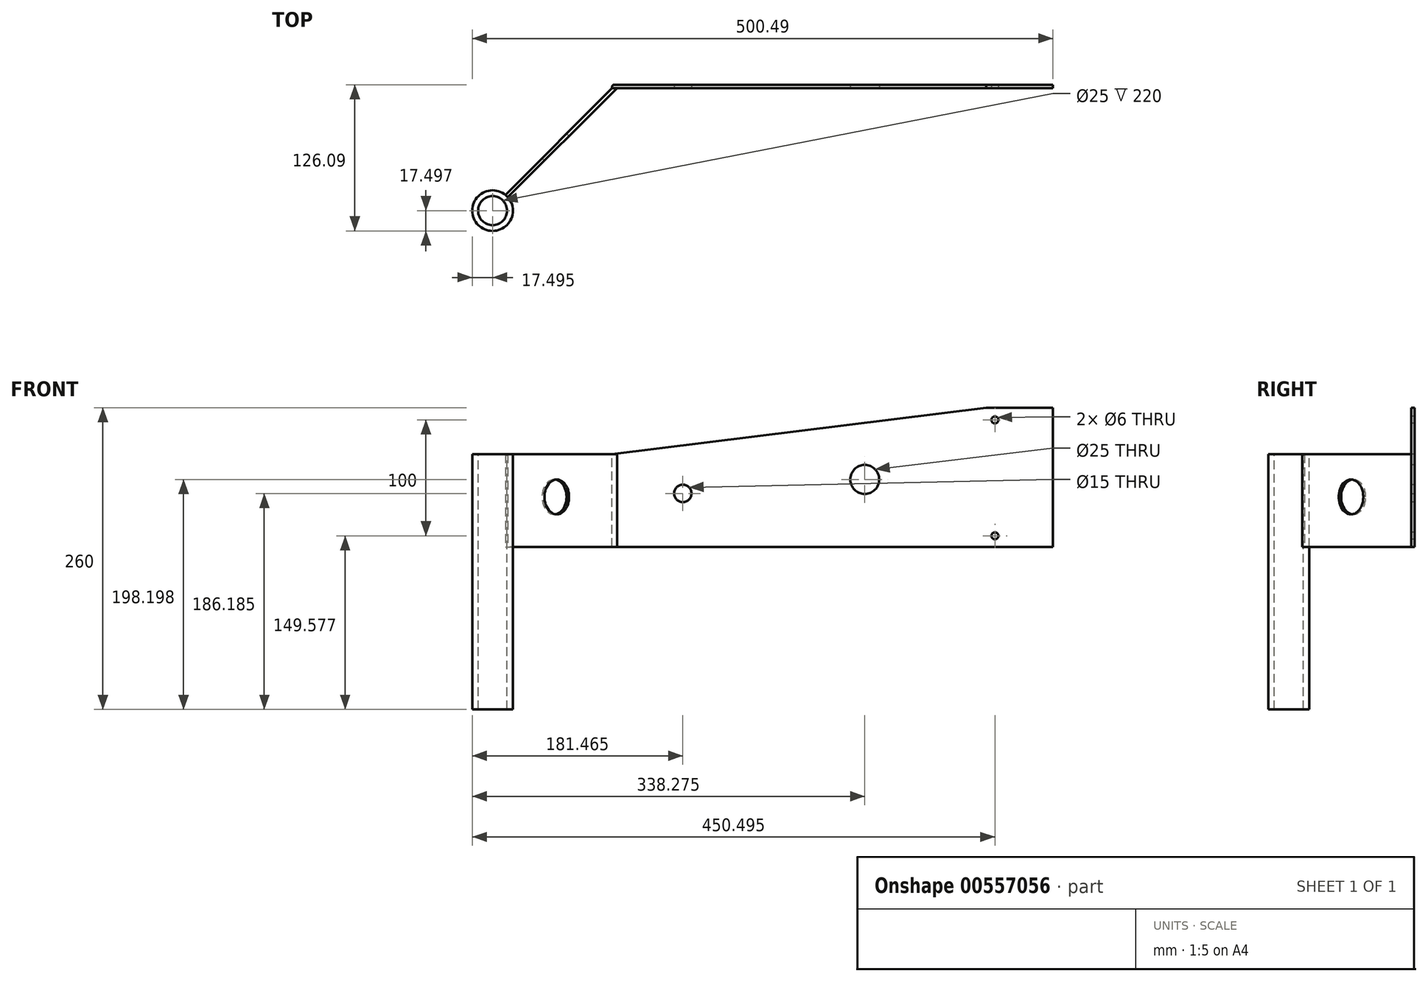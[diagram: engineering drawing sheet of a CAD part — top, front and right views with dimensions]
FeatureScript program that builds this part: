
annotation { "Feature Type Name" : "Feature", "Feature Type Description" : "" }
export const myFeature = defineFeature(function(context is Context, id is Id, definition is map)
    precondition{}
    {
        {
            var Q0;
            Q0=qCreatedBy(makeId("Front.planeOp"),FACE);
            var sketch = newSketch(context, id + "F0", { "sketchPlane" : qUnion([Q0])});
            skLineSegment(sketch, "E0.bottom", {"start": v(286.31, -3.5) * mm, "end": v(-93.69, -3.5) * mm});
            skLineSegment(sketch, "E0.top", {"start": v(286.31, 116.5) * mm, "end": v(228.84, 116.5) * mm});
            skLineSegment(sketch, "E0.left", {"start": v(286.31, -3.5) * mm, "end": v(286.31, 116.5) * mm});
            skLineSegment(sketch, "E0.right", {"start": v(-93.69, -3.5) * mm, "end": v(-93.69, 76.5) * mm});
            skLineSegment(sketch, "E1", {"start": v(-93.69, 76.5) * mm, "end": v(228.84, 116.5) * mm});
            skSolve(sketch);
        }
        {
            var Q0;
            Q0=makeQuery(id+"F0.imprint","IMPRINT",FACE,{"disambiguationData":[TD([[makeQuery(id+"F0.imprint","IMPRINT",EDGE,{"derivedFrom":sQuery(id+"F0.wireOp",EDGE,"E0.bottom")}),-1.0]])]});
            extrude(context, id + "F1", {"entities" : qUnion([Q0]), "depth" : 3 * mm, "offsetDistance" : 25 * mm});
        }
        {
            var Q0;
            Q0=makeQuery(id+"F1.opExtrude","SWEPT_FACE",FACE,{"disambiguationData":[OSD([sQuery(id+"F0.wireOp",EDGE,"E0.bottom")])]});
            var sketch = newSketch(context, id + "F2", { "sketchPlane" : qUnion([Q0])});
            skLineSegment(sketch, "E2", {"start": v(-93.69, 3) * mm, "end": v(-185.6, 94.92) * mm});
            skLineSegment(sketch, "E3", {"start": v(-185.6, 94.92) * mm, "end": v(-183.49, 97.05) * mm});
            skLineSegment(sketch, "E4", {"start": v(-183.49, 97.05) * mm, "end": v(-86.44, 0) * mm});
            skLineSegment(sketch, "E5", {"start": v(-93.69, 3) * mm, "end": v(-217, 3) * mm, "construction": true});
            skSolve(sketch);
        }
        {
            var Q0;
            {var subQ0=sQuery(id+"F2.wireOp",EDGE,"E2");Q0=makeQuery(id+"F2.imprint","IMPRINT",FACE,{"disambiguationData":[TD([[makeQuery(id+"F2.imprint","IMPRINT",EDGE,{"derivedFrom":subQ0}),-1.0]])]});}
            var sketch = newSketch(context, id + "F3", { "sketchPlane" : qUnion([Q0])});
            skSolve(sketch);
        }
        {
            var Q0;
            {var subQ0=sQuery(id+"F2.wireOp",EDGE,"E2");Q0=makeQuery(id+"F2.imprint","IMPRINT",FACE,{"disambiguationData":[TD([[makeQuery(id+"F2.imprint","IMPRINT",EDGE,{"derivedFrom":subQ0}),-1.0]])]});}
            extrude(context, id + "F4", {"entities" : qUnion([Q0]), "operationType" : NewBodyOperationType.ADD, "oppositeDirection" : true, "depth" : 80 * mm, "offsetDistance" : 25 * mm});
        }
        {
            var Q0;
            Q0=makeQuery(id+"F1.opExtrude","CAP_EDGE",EDGE,{"disambiguationData":[OSD([sQuery(id+"F0.wireOp",EDGE,"E0.right")])],"isStart":true});
            fillet(context, id + "F5", {"entities" : qUnion([Q0]), "radius" : 2 * mm, "tangentPropagation" : true, "allowEdgeOverflow" : false});
        }
        {
            var Q0;
            {var subQ0=sQuery(id+"F2.wireOp",EDGE,"E2");Q0=makeQuery(id+"F3.imprint","IMPRINT",FACE,{"disambiguationData":[TD([[makeQuery(id+"F3.imprint","IMPRINT",EDGE,{"derivedFrom":makeQuery(id+"F2.imprint","IMPRINT",EDGE,{"derivedFrom":subQ0})}),-1.0]])]});}
            extrude(context, id + "F6", {"entities" : qUnion([Q0]), "oppositeDirection" : true, "depth" : 80 * mm, "offsetDistance" : 25 * mm});
        }
        {
            var Q0;
            Q0=makeQuery(id+"F1.opExtrude","CAP_FACE",FACE,{"disambiguationData":[OSD([sQuery(id+"F0.wireOp",EDGE,"E0.bottom"),sQuery(id+"F0.wireOp",EDGE,"E0.top"),sQuery(id+"F0.wireOp",EDGE,"E0.left"),sQuery(id+"F0.wireOp",EDGE,"E0.right"),sQuery(id+"F0.wireOp",EDGE,"E1")])],"isStart":false});
            var sketch = newSketch(context, id + "F7", { "sketchPlane" : qUnion([Q0])});
            skCircle(sketch, "E6", {"center": v(124.1, 54.7) * mm, "radius": 12.5 * mm});
            skSolve(sketch);
        }
        {
            var Q0;
            Q0=makeQuery(id+"F7.imprint","IMPRINT",FACE,{"disambiguationData":[TD([[makeQuery(id+"F7.imprint","IMPRINT",EDGE,{"derivedFrom":sQuery(id+"F7.wireOp",EDGE,"E6")}),1.0]])]});
            extrude(context, id + "F8", {"entities" : qUnion([Q0]), "operationType" : NewBodyOperationType.REMOVE, "oppositeDirection" : true, "depth" : 3 * mm, "offsetDistance" : 25 * mm});
        }
        {
            var Q0;
            Q0=makeQuery(id+"F1.opExtrude","CAP_FACE",FACE,{"disambiguationData":[OSD([sQuery(id+"F0.wireOp",EDGE,"E0.bottom"),sQuery(id+"F0.wireOp",EDGE,"E0.top"),sQuery(id+"F0.wireOp",EDGE,"E0.left"),sQuery(id+"F0.wireOp",EDGE,"E0.right"),sQuery(id+"F0.wireOp",EDGE,"E1")])],"isStart":false});
            var sketch = newSketch(context, id + "F9", { "sketchPlane" : qUnion([Q0])});
            skCircle(sketch, "E7", {"center": v(-32.71, 42.7) * mm, "radius": 7.5 * mm});
            skSolve(sketch);
        }
        {
            var Q0;
            Q0=makeQuery(id+"F9.imprint","IMPRINT",FACE,{"disambiguationData":[TD([[makeQuery(id+"F9.imprint","IMPRINT",EDGE,{"derivedFrom":sQuery(id+"F9.wireOp",EDGE,"E7")}),1.0]])]});
            extrude(context, id + "F10", {"entities" : qUnion([Q0]), "operationType" : NewBodyOperationType.REMOVE, "endBound" : BoundingType.THROUGH_ALL, "oppositeDirection" : true, "depth" : 3 * mm, "offsetDistance" : 25 * mm});
        }
        {
            var Q0;
            Q0=makeQuery(id+"F1.opExtrude","CAP_FACE",FACE,{"disambiguationData":[OSD([sQuery(id+"F0.wireOp",EDGE,"E0.bottom"),sQuery(id+"F0.wireOp",EDGE,"E0.top"),sQuery(id+"F0.wireOp",EDGE,"E0.left"),sQuery(id+"F0.wireOp",EDGE,"E0.right"),sQuery(id+"F0.wireOp",EDGE,"E1")])],"isStart":false});
            var sketch = newSketch(context, id + "F11", { "sketchPlane" : qUnion([Q0])});
            skLineSegment(sketch, "E8", {"start": v(-33, 35.2) * mm, "end": v(124.65, 42.22) * mm});
            skLineSegment(sketch, "E9", {"start": v(-33.27, 50.17) * mm, "end": v(125.22, 67.4) * mm});
            skSolve(sketch);
        }
        {
            var Q0;
            {var subQ0=sQuery(id+"F11.wireOp",EDGE,"E8");var subQ1=makeQuery(id+"F8.boolean.opBoolean","COPY",EDGE,{"derivedFrom":makeQuery(id+"F8.opExtrude","CAP_EDGE",EDGE,{"disambiguationData":[OSD([sQuery(id+"F7.wireOp",EDGE,"E6")])],"isStart":true})});var subQ2=makeQuery(id+"F11.imprint","INTERSECT",VERTEX,{"derivedFrom":[subQ1,subQ0]});Q0=makeQuery(id+"F11.imprint","IMPRINT",FACE,{"disambiguationData":[TD([[makeQuery(id+"F11.imprint","IMPRINT",EDGE,{"disambiguationData":[TD([[subQ2,1.0]])],"derivedFrom":subQ0}),1.0]])]});}
            extrude(context, id + "F12", {"entities" : qUnion([Q0]), "operationType" : NewBodyOperationType.REMOVE, "oppositeDirection" : true, "depth" : 3 * mm, "offsetDistance" : 25 * mm});
        }
        {
            var Q0;
            Q0=makeQuery(id+"F4.opExtrude","SWEPT_FACE",FACE,{"disambiguationData":[OSD([sQuery(id+"F2.wireOp",EDGE,"E4")])]});
            var sketch = newSketch(context, id + "F13", { "sketchPlane" : qUnion([Q0])});
            skCircle(sketch, "E10", {"center": v(-138.84, 39.67) * mm, "radius": 15 * mm});
            skSolve(sketch);
        }
        {
            var Q0;
            Q0=makeQuery(id+"F1.opExtrude","CAP_FACE",FACE,{"disambiguationData":[OSD([sQuery(id+"F0.wireOp",EDGE,"E0.bottom"),sQuery(id+"F0.wireOp",EDGE,"E0.top"),sQuery(id+"F0.wireOp",EDGE,"E0.left"),sQuery(id+"F0.wireOp",EDGE,"E0.right"),sQuery(id+"F0.wireOp",EDGE,"E1")])],"isStart":false});
            var sketch = newSketch(context, id + "F14", { "sketchPlane" : qUnion([Q0])});
            skLineSegment(sketch, "E11", {"start": v(286.31, 116.5) * mm, "end": v(236.31, 116.5) * mm});
            skLineSegment(sketch, "E12", {"start": v(236.31, 116.5) * mm, "end": v(236.31, 106.09) * mm});
            skCircle(sketch, "E13", {"center": v(236.31, 106.09) * mm, "radius": 3 * mm});
            skSolve(sketch);
        }
        {
            var Q0;
            Q0=makeQuery(id+"F14.imprint","IMPRINT",FACE,{"disambiguationData":[TD([[makeQuery(id+"F14.imprint","IMPRINT",EDGE,{"derivedFrom":sQuery(id+"F14.wireOp",EDGE,"E13")}),1.0]])]});
            extrude(context, id + "F15", {"entities" : qUnion([Q0]), "operationType" : NewBodyOperationType.REMOVE, "endBound" : BoundingType.THROUGH_ALL, "oppositeDirection" : true, "depth" : 3 * mm, "offsetDistance" : 25 * mm});
        }
        {
            var Q0;
            Q0=makeQuery(id+"F1.opExtrude","CAP_FACE",FACE,{"disambiguationData":[OSD([sQuery(id+"F0.wireOp",EDGE,"E0.bottom"),sQuery(id+"F0.wireOp",EDGE,"E0.top"),sQuery(id+"F0.wireOp",EDGE,"E0.left"),sQuery(id+"F0.wireOp",EDGE,"E0.right"),sQuery(id+"F0.wireOp",EDGE,"E1")])],"isStart":false});
            var sketch = newSketch(context, id + "F16", { "sketchPlane" : qUnion([Q0])});
            skLineSegment(sketch, "E14", {"start": v(236.31, 106.09) * mm, "end": v(236.31, 6.09) * mm});
            skCircle(sketch, "E15", {"center": v(236.31, 6.09) * mm, "radius": 3 * mm});
            skSolve(sketch);
        }
        {
            var Q0;
            Q0=makeQuery(id+"F16.imprint","IMPRINT",FACE,{"disambiguationData":[TD([[makeQuery(id+"F16.imprint","IMPRINT",EDGE,{"derivedFrom":sQuery(id+"F16.wireOp",EDGE,"E15")}),1.0]])]});
            extrude(context, id + "F17", {"entities" : qUnion([Q0]), "operationType" : NewBodyOperationType.REMOVE, "endBound" : BoundingType.THROUGH_ALL, "oppositeDirection" : true, "depth" : 25 * mm, "offsetDistance" : 25 * mm});
        }
        {
            var Q0;
            {var subQ0=sQuery(id+"F2.wireOp",EDGE,"E2");Q0=makeQuery(id+"F2.imprint","IMPRINT",FACE,{"disambiguationData":[TD([[makeQuery(id+"F2.imprint","IMPRINT",EDGE,{"derivedFrom":subQ0}),-1.0]])]});}
            extrude(context, id + "F18", {"entities" : qUnion([Q0]), "operationType" : NewBodyOperationType.ADD, "oppositeDirection" : true, "depth" : 80 * mm, "offsetDistance" : 25 * mm});
        }
        {
            var Q0;
            Q0=makeQuery(id+"F13.imprint","IMPRINT",FACE,{"disambiguationData":[TD([[makeQuery(id+"F13.imprint","IMPRINT",EDGE,{"derivedFrom":sQuery(id+"F13.wireOp",EDGE,"E10")}),1.0]])]});
            extrude(context, id + "F19", {"entities" : qUnion([Q0]), "operationType" : NewBodyOperationType.REMOVE, "endBound" : BoundingType.THROUGH_ALL, "oppositeDirection" : true, "depth" : 25 * mm, "offsetDistance" : 25 * mm});
        }
        {
            var Q0;
            Q0=makeQuery(id+"F4.opExtrude","CAP_FACE",FACE,{"disambiguationData":[OSD([sQuery(id+"F0.wireOp",EDGE,"E0.bottom"),sQuery(id+"F2.wireOp",EDGE,"E2"),sQuery(id+"F2.wireOp",EDGE,"E3"),sQuery(id+"F2.wireOp",EDGE,"E4")])],"isStart":false});
            var sketch = newSketch(context, id + "F20", { "sketchPlane" : qUnion([Q0])});
            skCircle(sketch, "E16", {"center": v(-196.68, -108.6) * mm, "radius": 17.5 * mm});
            skSolve(sketch);
        }
        {
            var Q0;
            Q0=makeQuery(id+"F20.imprint","IMPRINT",FACE,{"disambiguationData":[TD([[makeQuery(id+"F20.imprint","IMPRINT",EDGE,{"derivedFrom":sQuery(id+"F20.wireOp",EDGE,"E16")}),1.0]])]});
            extrude(context, id + "F21", {"entities" : qUnion([Q0]), "oppositeDirection" : true, "depth" : 220 * mm, "offsetDistance" : 25 * mm});
        }
        {
            var Q0;
            Q0=makeQuery(id+"F21.opExtrude","CAP_FACE",FACE,{"disambiguationData":[OSD([sQuery(id+"F20.wireOp",EDGE,"E16")])],"isStart":true});
            var sketch = newSketch(context, id + "F22", { "sketchPlane" : qUnion([Q0])});
            skCircle(sketch, "E17", {"center": v(-196.68, -108.6) * mm, "radius": 12.5 * mm});
            skSolve(sketch);
        }
        {
            var Q0;
            Q0=makeQuery(id+"F22.imprint","IMPRINT",FACE,{"disambiguationData":[TD([[makeQuery(id+"F22.imprint","IMPRINT",EDGE,{"derivedFrom":sQuery(id+"F22.wireOp",EDGE,"E17")}),1.0]])]});
            extrude(context, id + "F23", {"entities" : qUnion([Q0]), "operationType" : NewBodyOperationType.REMOVE, "endBound" : BoundingType.THROUGH_ALL, "oppositeDirection" : true, "depth" : 220 * mm, "offsetDistance" : 25 * mm});
        }
        {
            var Q0;
            Q0=makeQuery(id+"F21.opExtrude","SWEPT_BODY",BODY,{"disambiguationData":[OSD([sQuery(id+"F20.wireOp",EDGE,"E16")])]});
            var Q1;
            Q1=qCreatedBy(makeId("Right.planeOp"),FACE);
            mirror(context, id + "F24", {"entities" : qUnion([Q0]), "mirrorPlane" : qUnion([Q1])});
        }
        {
            var Q0;
            Q0=makeQuery(id+"F24.opPattern","COPY",BODY,{"derivedFrom":makeQuery(id+"F21.opExtrude","SWEPT_BODY",BODY,{"disambiguationData":[OSD([sQuery(id+"F20.wireOp",EDGE,"E16")])]}),"instanceName":"1"});
            deleteBodies(context, id + "F25", {"entities" : qUnion([Q0])});
        }
    });
